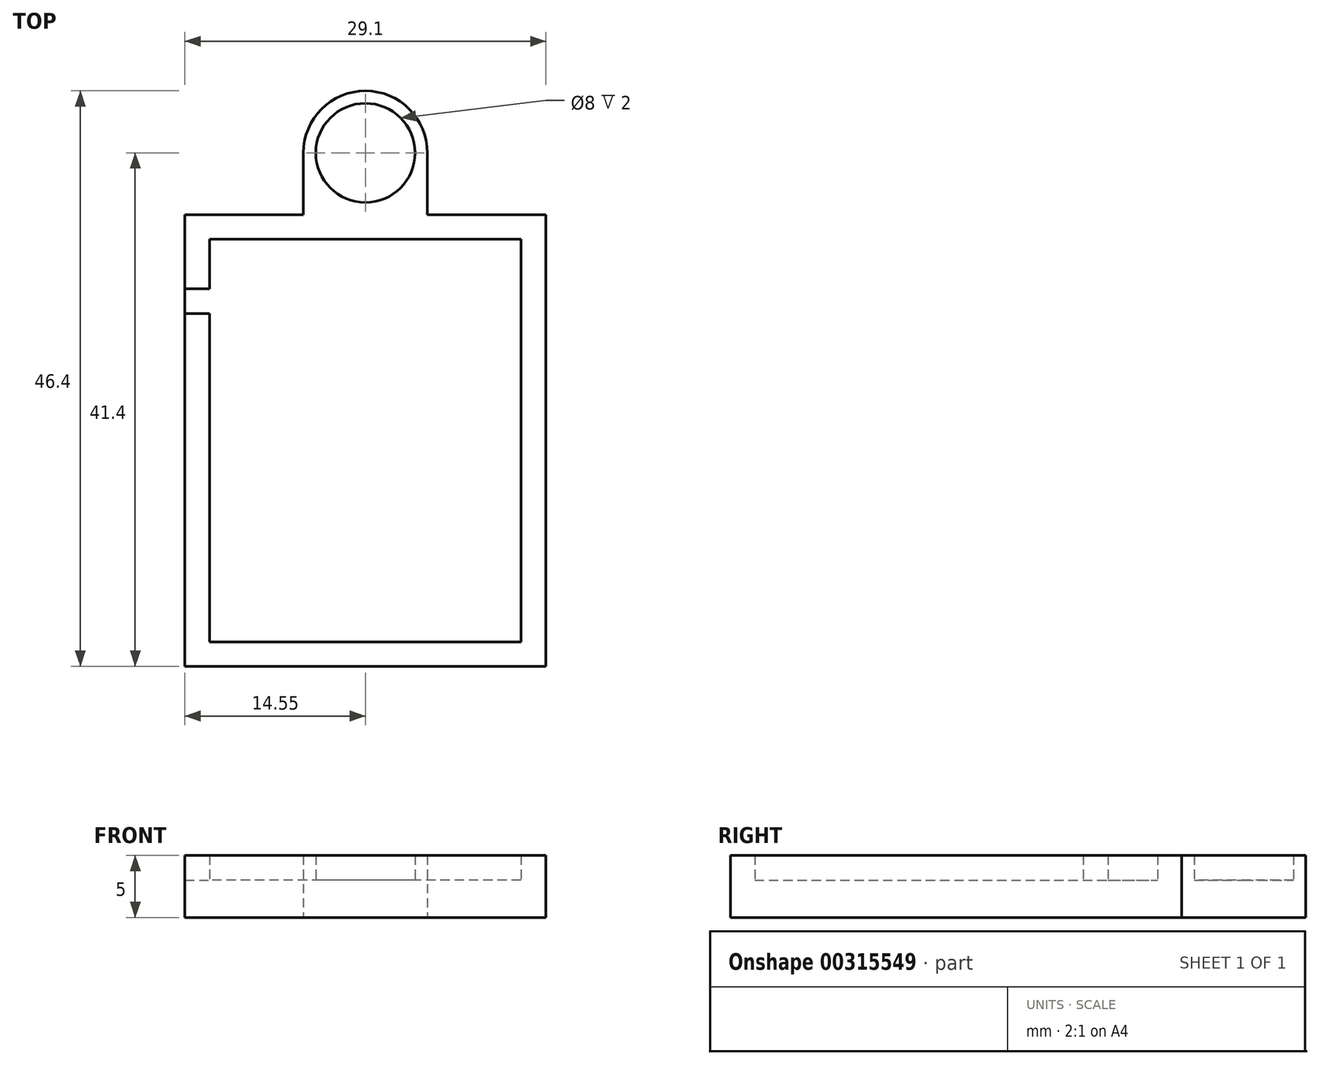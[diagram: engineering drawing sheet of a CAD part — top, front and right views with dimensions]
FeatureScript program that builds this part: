
annotation { "Feature Type Name" : "Feature", "Feature Type Description" : "" }
export const myFeature = defineFeature(function(context is Context, id is Id, definition is map)
    precondition{}
    {
        {
            var Q0;
            Q0=qCreatedBy(makeId("Top.planeOp"),FACE);
            var sketch = newSketch(context, id + "F0", { "sketchPlane" : qUnion([Q0])});
            skLineSegment(sketch, "E0.bottom", {"start": v(12.55, -16.24) * mm, "end": v(-12.55, -16.24) * mm});
            skLineSegment(sketch, "E0.top", {"start": v(12.55, 16.24) * mm, "end": v(-12.55, 16.24) * mm});
            skLineSegment(sketch, "E0.left", {"start": v(12.55, -16.24) * mm, "end": v(12.55, 16.24) * mm});
            skLineSegment(sketch, "E0.right", {"start": v(-12.55, -16.24) * mm, "end": v(-12.55, 10.24) * mm});
            skPoint(sketch, "E0.middle", {"position": v(0, 0) * mm});
            skLineSegment(sketch, "E1.bottom", {"start": v(14.55, -18.2) * mm, "end": v(-14.55, -18.2) * mm});
            skLineSegment(sketch, "E1.top", {"start": v(14.55, 18.2) * mm, "end": v(-14.55, 18.2) * mm});
            skLineSegment(sketch, "E1.left", {"start": v(14.55, -18.2) * mm, "end": v(14.55, 18.2) * mm});
            skLineSegment(sketch, "E1.right", {"start": v(-14.55, -18.2) * mm, "end": v(-14.55, 10.24) * mm});
            skLineSegment(sketch, "E2", {"start": v(-12.55, 16.24) * mm, "end": v(-12.55, 12.24) * mm});
            skLineSegment(sketch, "E3", {"start": v(-12.55, 10.24) * mm, "end": v(-14.55, 10.24) * mm});
            skLineSegment(sketch, "E4", {"start": v(-14.55, 12.24) * mm, "end": v(-12.55, 12.24) * mm});
            skPoint(sketch, "E5.orphan", {"position": v(-12.55, 11.24) * mm});
            skLineSegment(sketch, "E6.trimOffspring", {"start": v(-12.55, 12.24) * mm, "end": v(-12.55, 16.24) * mm});
            skLineSegment(sketch, "E7.trimOffspring", {"start": v(-14.55, 12.24) * mm, "end": v(-14.55, 18.2) * mm});
            skPoint(sketch, "E8.start.orphan", {"position": v(-14.55, 11.24) * mm});
            skLineSegment(sketch, "E9", {"start": v(-12.55, 12.24) * mm, "end": v(-12.55, 10.24) * mm});
            skLineSegment(sketch, "E10", {"start": v(-14.55, 12.24) * mm, "end": v(-14.55, 10.24) * mm});
            skPoint(sketch, "E11.endSnap0", {"position": v(0, 18.2) * mm});
            skCircle(sketch, "E12", {"center": v(0, 23.2) * mm, "radius": 5 * mm});
            skLineSegment(sketch, "E13", {"start": v(5, 23.2) * mm, "end": v(5, 18.2) * mm});
            skLineSegment(sketch, "E14", {"start": v(-5, 23.2) * mm, "end": v(-5, 18.2) * mm});
            skCircle(sketch, "E15", {"center": v(0, 23.2) * mm, "radius": 4 * mm});
            skLineSegment(sketch, "E16", {"start": v(15.55, 19.2) * mm, "end": v(5, 19.2) * mm});
            skLineSegment(sketch, "E17", {"start": v(2.48, -19.2) * mm, "end": v(15.55, -19.2) * mm});
            skLineSegment(sketch, "E18", {"start": v(15.55, 19.2) * mm, "end": v(15.55, -19.2) * mm});
            skLineSegment(sketch, "E19.0", {"start": v(15.55, 20.2) * mm, "end": v(5, 20.2) * mm});
            skLineSegment(sketch, "E20.0", {"start": v(2.48, -20.2) * mm, "end": v(15.55, -20.2) * mm});
            skLineSegment(sketch, "E21.0", {"start": v(16.55, 19.2) * mm, "end": v(16.55, -19.2) * mm});
            skLineSegment(sketch, "E22", {"start": v(15.55, 20.2) * mm, "end": v(16.55, 20.2) * mm});
            skLineSegment(sketch, "E23", {"start": v(16.55, 20.2) * mm, "end": v(16.55, 19.2) * mm});
            skLineSegment(sketch, "E24", {"start": v(15.55, -20.2) * mm, "end": v(16.55, -20.2) * mm});
            skLineSegment(sketch, "E25", {"start": v(16.55, -20.2) * mm, "end": v(16.55, -19.2) * mm});
            skLineSegment(sketch, "E26", {"start": v(2.48, -20.2) * mm, "end": v(2.48, -19.2) * mm});
            skLineSegment(sketch, "E27", {"start": v(2.48, -18.2) * mm, "end": v(2.48, -19.2) * mm});
            skSolve(sketch);
        }
        {
            var Q0;
            Q0=makeQuery(id+"F0.imprint","IMPRINT",FACE,{"disambiguationData":[TD([[makeQuery(id+"F0.imprint","IMPRINT",EDGE,{"derivedFrom":sQuery(id+"F0.wireOp",EDGE,"E0.bottom")}),-1.0]])]});
            var Q1;
            Q1=makeQuery(id+"F0.imprint","IMPRINT",FACE,{"disambiguationData":[TD([[makeQuery(id+"F0.imprint","IMPRINT",EDGE,{"derivedFrom":sQuery(id+"F0.wireOp",EDGE,"E15")}),1.0]])]});
            extrude(context, id + "F1", {"entities" : qUnion([Q0, Q1]), "depth" : 3 * mm});
        }
        {
            var Q0;
            Q0=makeQuery(id+"F0.imprint","IMPRINT",FACE,{"disambiguationData":[TD([[makeQuery(id+"F0.imprint","IMPRINT",EDGE,{"derivedFrom":sQuery(id+"F0.wireOp",EDGE,"E0.bottom")}),1.0]])]});
            var Q1;
            Q1=makeQuery(id+"F0.imprint","IMPRINT",FACE,{"disambiguationData":[TD([[makeQuery(id+"F0.imprint","IMPRINT",EDGE,{"derivedFrom":sQuery(id+"F0.wireOp",EDGE,"E15")}),-1.0]])]});
            var Q2;
            {var subQ0=sQuery(id+"F0.wireOp",EDGE,"E13");Q2=makeQuery(id+"F0.imprint","IMPRINT",FACE,{"disambiguationData":[TD([[makeQuery(id+"F0.imprint","IMPRINT",EDGE,{"derivedFrom":subQ0}),-1.0]])]});}
            var Q3;
            {var subQ0=sQuery(id+"F0.wireOp",EDGE,"E14");Q3=makeQuery(id+"F0.imprint","IMPRINT",FACE,{"disambiguationData":[TD([[makeQuery(id+"F0.imprint","IMPRINT",EDGE,{"derivedFrom":subQ0}),1.0]])]});}
            extrude(context, id + "F2", {"entities" : qUnion([Q0, Q1, Q2, Q3]), "operationType" : NewBodyOperationType.ADD, "depth" : 5 * mm});
        }
        {
            var Q0;
            Q0=makeQuery(id+"F1.opExtrude","SWEPT_FACE",FACE,{"disambiguationData":[OSD([sQuery(id+"F0.wireOp",EDGE,"E0.right"),sQuery(id+"F0.wireOp",EDGE,"E6.trimOffspring"),sQuery(id+"F0.wireOp",EDGE,"E9")])]});
            extrude(context, id + "F3", {"entities" : qUnion([Q0]), "operationType" : NewBodyOperationType.ADD, "depth" : 2 * mm});
        }
    });
